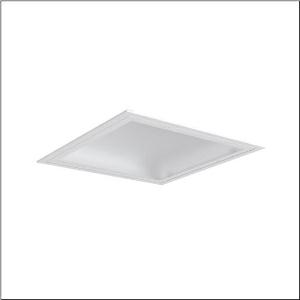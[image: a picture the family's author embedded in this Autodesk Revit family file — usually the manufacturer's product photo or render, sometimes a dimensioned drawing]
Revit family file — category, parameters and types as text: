
# Revit family: mira_r__21_51fr427a472a_c216
name_source: partatom
category: Lighting Fixtures
units: mm (PartAtom-declared; Revit-internal decimal feet)

## family parameters
Cut with Voids When Loaded = No
Host = Face
Light Source = No
Part Type = Normal
Room Calculation Point = No
Round Connector Dimension = Use Diameter
Shared = No

## types (1)
- Mira® 21 (1 x LED, 7680 lm, 66 W, 4000K)
    Apparent Load = 66 VA
    CIE Flux Codes = 50 81 97 100 100
    Color Rendering = 80
    Color Temperature = 4000K
    Default Elevation = 1800 mm
    Description = Mira® 21, clean room luminaire, primary light control with reflector, primary optical cover: cover, of PC, light emission: direct distribution, primary light characteristic: symmetric, installation type: recessed, LED, rated luminous flux: 7.680lm, luminous efficacy: 116lm/W, light colour: 840, colour temperature: 4000K, control gear: ECG, with terminal, 3-pole, max. 2.5mm², mains connection: 230V, AC, 50/60Hz, rated input power: 66W, luminaire housing, of sheet steel, coated, pure white (RAL 9010), with concealed spring brackets, module: M625, length: 623mm, width: 623mm, height: 115mm, protection rating (complete): IP54, insulation class (complete): insulation class I (protective earthing), certification: CE, UKCA, permissible operating ambient temperature: -5..+40°C, standard: EN 50419, packaging unit: 1 piece
    Height = 0 mm  [stored 0 ft]
    Lamp = 1 x LED
    Lamp Light Flux = 7680 lm
    Lamp Power = 66 W
    Lamp count = 1
    Length = 625 mm
    Luminous efficacy = 116 lm/W
    Manufacturer = Siteco
    ModVariant = No
    Model = 51FR427A472A
    Mounting Place = Ceiling
    Mounting Type = Recessed
    Number of Poles = 1
    OnlyDefault = Yes
    Power Factor = 1
    Product Name = Mira® 21
    Product group = clean room luminaire
    ProductGroupID = 402
    Protection Class = Protection class I
    Protection Degree = IP 54
    RLX_Detail_Level = 1
    RLX_Emergency_Light_Flux = 0 lm
    RLX_Emergency_Type = 0
    RLX_Emergency_Type_DB = No
    RlxData = <blob elided: 13369 chars, md5=2a2e75bf>
    Socket = socket
    Standby Power = 0 W
    System Light Flux = 7680 lm
    System Power = 66 W
    Type Comments = Product without accessories
    Type Image = l_1007109.jpg
    URL = http://relux.com
    VarID = ---
    Voltage = 0 V
    Weight = 0.00 kg
    Width = 625 mm

note: [stored X ft] marks values corroborated as IEEE doubles in the binary element streams (Revit-internal decimal feet)

## geometry (parser evidence)
native form markers: Sweep x12
no freeform markers — native parametric forms only
